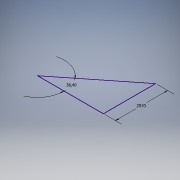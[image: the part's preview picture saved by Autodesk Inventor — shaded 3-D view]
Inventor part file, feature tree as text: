
AUTODESK INVENTOR PART (.ipt)
format: ipt  version: 2018 (Build 220112000, 112)  size: 85,504 bytes
history: native  units: mm
features: sketch x1
ambient origin geometry x8: Origin, YZ Plane, XZ Plane, XY Plane, X Axis, Y Axis, Z Axis, Center Point
feature tree (1):
  sketch  "Sketch1"  dims[d0=2970.0mm d1=6.702064mm]
